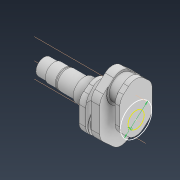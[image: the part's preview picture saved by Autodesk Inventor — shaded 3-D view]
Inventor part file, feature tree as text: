
AUTODESK INVENTOR PART (.ipt)
format: ipt  version: 2022 (Build 260153000, 153)  size: 330,240 bytes
history: native  units: mm
features: sketch x14, extrude x12, projected_geometry x4, other x3, revolve x1
ambient origin geometry x8: Origin, YZ Plane, XZ Plane, XY Plane, X Axis, Y Axis, Z Axis, Center Point
bodies: Solid1 (feature_tree)
feature tree (34):
  revolve  "Revolution1"  [1 undecoded]
  sketch  "Sketch3"  dims[d3=44.0mm d4=36.0mm]
  extrude  "Extrusion6"  Depth=44.0mm
  extrude  "Extrusion7"  Depth=42.0mm
  extrude  "Extrusion8"  Depth=25.5mm
  extrude  "Extrusion9"  TaperAngle=90.0deg  [1 undecoded]
  extrude  "Extrusion10"  Depth=50.0mm
  extrude  "Extrusion11"  Depth=25.0mm
  extrude  "Extrusion12"  Depth=74.0mm
  extrude  "Extrusion13"  Depth=2.0mm
  extrude  "Extrusion14"  Depth=14.76mm TaperAngle=0.0deg
  extrude  "Extrusion15"  Depth=28.965484mm
  extrude  "Extrusion16"  Depth=32.5mm
  extrude  "Extrusion17"  Depth=1.0mm
  sketch  "Sketch21"  dims[d62=21.0mm d63=0.0mm d64=65.0mm d65=1.0mm d66=0.0mm d67=25.0mm d68=55.4mm d71=30.36mm d72=95.0mm d73=18.91mm d74=0.0mm d76=32.5mm d77=13.55mm d78=1.0mm d79=0.0mm d80=55.0mm d81=21.0mm d82=0.0mm d83=2.0mm d84=0.0mm d85=65.0mm d86=1.0mm d87=0.0mm d88=15.0mm d89=25.0mm d90=40.4mm d91=10.43mm d92=0.0mm d93=10.43mm d94=0.0mm d95=70.0mm d41=0.5mm d42=0.872665mm d43=0.5mm d44=0.872665mm]
  other  "Work Axis1"
  other  "Work Axis2"
  other  "Work Axis3"
  sketch  "Sketch1"  dims[d1=23.0mm d2=23.0mm]
  sketch  "Sketch10"  dims[d6=40.0mm d7=42.0mm]
  sketch  "Sketch11"  dims[d9=25.5mm d10=2.0mm]
  sketch  "Sketch12"  dims[d11=1.5mm d12=90.0deg]
  sketch  "Sketch13"  dims[d13=65.0mm d14=50.0mm]
  projected_geometry  "Projected Loop5"
  sketch  "Sketch14"  dims[d15=1.0mm d17=25.0mm]
  sketch  "Sketch15"  dims[d18=74.0mm d19=36.4mm]
  sketch  "Sketch16"  dims[d21=14.88mm d24=2.0mm]
  projected_geometry  "Projected Loop6"
  sketch  "Sketch17"  dims[d50=14.88mm d51=14.76mm d52=0.0mm]
  projected_geometry  "Projected Loop7"
  sketch  "Sketch18"  dims[d53=10.3mm d54=28.965484mm]
  sketch  "Sketch19"  dims[d55=0.0mm d56=0.0mm d58=32.5mm]
  sketch  "Sketch20"  dims[d59=1.0mm d60=0.0mm d61=55.0mm]
  projected_geometry  "Projected Loop8"
note: 2 required parameter values undecoded (feature->parameter linkage not recoverable at this tier; creation-order binding heuristic only, values carry confidence <= 0.55)